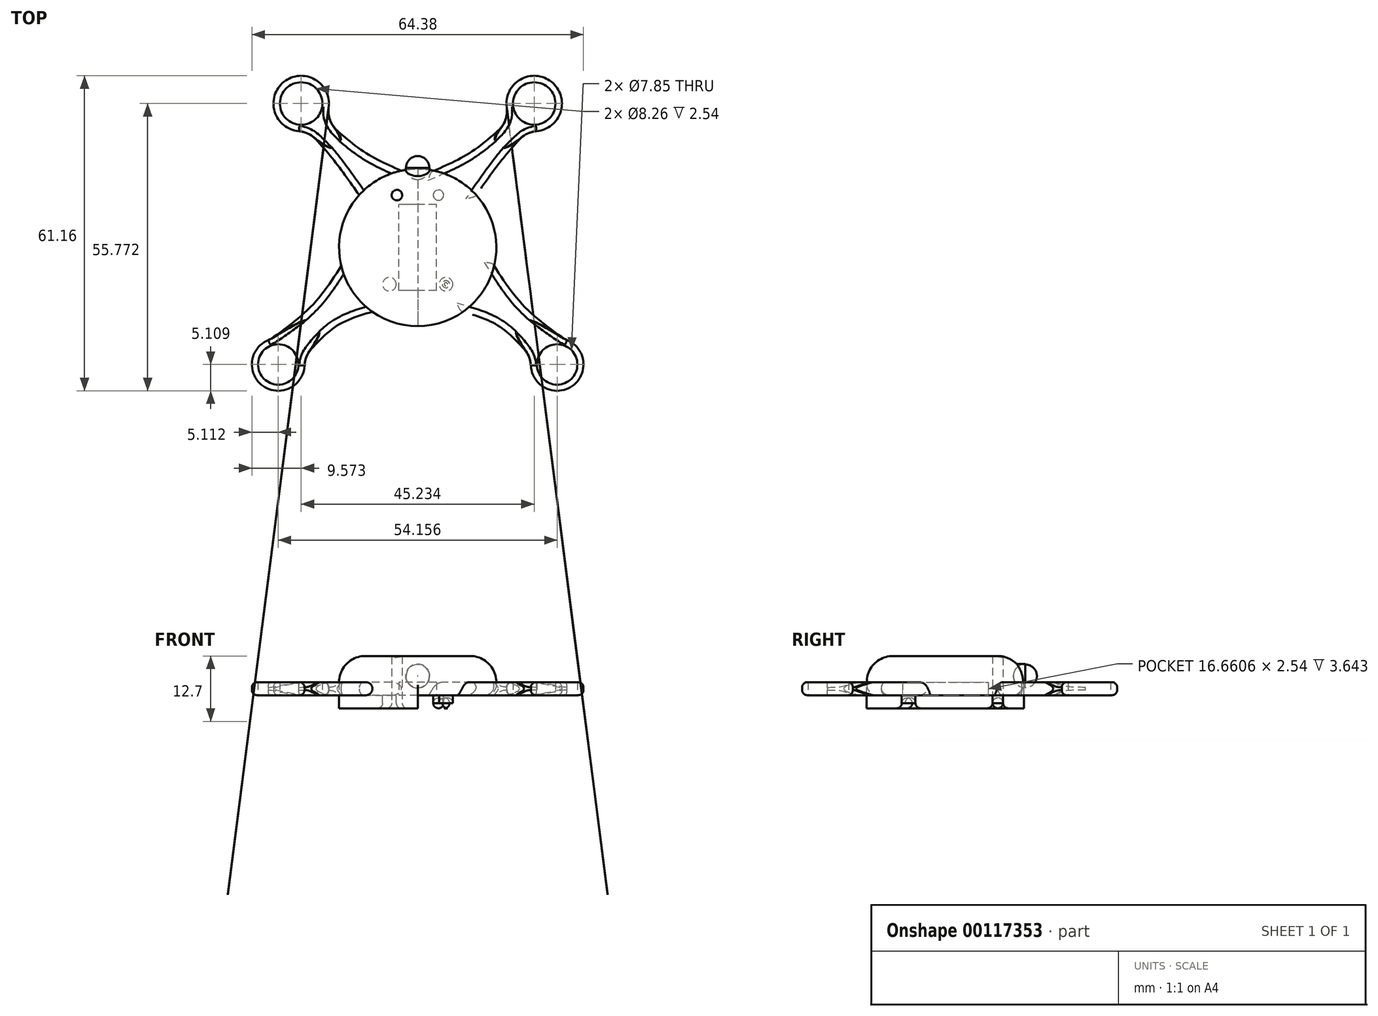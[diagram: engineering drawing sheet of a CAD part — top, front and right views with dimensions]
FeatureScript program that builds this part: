
annotation { "Feature Type Name" : "Feature", "Feature Type Description" : "" }
export const myFeature = defineFeature(function(context is Context, id is Id, definition is map)
    precondition{}
    {
        {
            var Q0;
            Q0=qCreatedBy(makeId("Top.planeOp"),FACE);
            var sketch = newSketch(context, id + "F0", { "sketchPlane" : qUnion([Q0])});
            skCircle(sketch, "E0", {"center": v(0, 0) * mm, "radius": 15.26 * mm});
            skLineSegment(sketch, "E1", {"start": v(9.1, 12.24) * mm, "end": v(22.62, 27.96) * mm});
            skCircle(sketch, "E2", {"center": v(22.62, 27.96) * mm, "radius": 5.39 * mm});
            skLineSegment(sketch, "E3", {"start": v(12.36, -8.95) * mm, "end": v(27.08, -22.7) * mm});
            skCircle(sketch, "E4", {"center": v(27.08, -22.7) * mm, "radius": 5.1 * mm});
            skFitSpline(sketch, "E5", {"points": [v(3.15, 14.93) * mm, v(10.13, 18.4) * mm, v(18.14, 24.96) * mm], "startDerivative": vector(15.03, 6.4) * mm, "endDerivative": vector(14.97, 13.52) * mm});
            skFitSpline(sketch, "E6", {"points": [v(11.37, 10.18) * mm, v(16.5, 17.24) * mm, v(21.38, 22.72) * mm], "startDerivative": vector(9.78, 14.08) * mm, "endDerivative": vector(10.27, 10.98) * mm});
            skFitSpline(sketch, "E7", {"points": [v(14.84, -3.54) * mm, v(20.44, -11.18) * mm, v(28.53, -17.8) * mm], "startDerivative": vector(10.46, -16.33) * mm, "endDerivative": vector(16.89, -12.25) * mm});
            skFitSpline(sketch, "E8", {"points": [v(8.8, -12.47) * mm, v(15.72, -15.22) * mm, v(22.14, -21.38) * mm], "startDerivative": vector(15.02, -4.3) * mm, "endDerivative": vector(11.73, -13.38) * mm});
            skCircle(sketch, "E9", {"center": v(4.03, 10.18) * mm, "radius": 1.02 * mm});
            skCircle(sketch, "E10", {"center": v(5.49, -7.13) * mm, "radius": 1.33 * mm});
            skLineSegment(sketch, "E11", {"start": v(0, 32.08) * mm, "end": v(0, -24.83) * mm});
            skFitSpline(sketch, "E12.MirrorCS", {"points": [v(-3.15, 14.93) * mm, v(-10.13, 18.4) * mm, v(-18.14, 24.96) * mm], "startDerivative": vector(-15.03, 6.4) * mm, "endDerivative": vector(-14.97, 13.52) * mm});
            skCircle(sketch, "E13.MirrorC", {"center": v(-22.62, 27.96) * mm, "radius": 5.39 * mm});
            skFitSpline(sketch, "E14.MirrorCS", {"points": [v(-14.84, -3.54) * mm, v(-20.44, -11.18) * mm, v(-28.53, -17.8) * mm], "startDerivative": vector(-10.46, -16.33) * mm, "endDerivative": vector(-16.89, -12.25) * mm});
            skLineSegment(sketch, "E15.MirrorCS", {"start": v(-12.36, -8.95) * mm, "end": v(-27.08, -22.7) * mm});
            skFitSpline(sketch, "E16.MirrorCS", {"points": [v(-8.8, -12.47) * mm, v(-15.72, -15.22) * mm, v(-22.14, -21.38) * mm], "startDerivative": vector(-15.02, -4.3) * mm, "endDerivative": vector(-11.73, -13.38) * mm});
            skCircle(sketch, "E17.MirrorC", {"center": v(-27.08, -22.7) * mm, "radius": 5.1 * mm});
            skLineSegment(sketch, "E18.MirrorCS", {"start": v(-9.1, 12.24) * mm, "end": v(-22.62, 27.96) * mm});
            skFitSpline(sketch, "E19.MirrorCS", {"points": [v(-11.37, 10.18) * mm, v(-16.5, 17.24) * mm, v(-21.38, 22.72) * mm], "startDerivative": vector(-9.78, 14.08) * mm, "endDerivative": vector(-10.27, 10.98) * mm});
            skCircle(sketch, "E20.MirrorC", {"center": v(-5.49, -7.13) * mm, "radius": 1.33 * mm});
            skCircle(sketch, "E21.MirrorC", {"center": v(-4.03, 10.18) * mm, "radius": 1.02 * mm});
            skCircle(sketch, "E22", {"center": v(27.08, -22.7) * mm, "radius": 3.93 * mm});
            skCircle(sketch, "E23", {"center": v(22.62, 27.96) * mm, "radius": 4.13 * mm});
            skCircle(sketch, "E24.MirrorC", {"center": v(-22.62, 27.96) * mm, "radius": 4.13 * mm});
            skCircle(sketch, "E25.MirrorC", {"center": v(-27.08, -22.7) * mm, "radius": 3.93 * mm});
            skSolve(sketch);
        }
        {
            var Q0;
            Q0=makeQuery(id+"F0.imprint","IMPRINT",FACE,{"disambiguationData":[TD([[makeQuery(id+"F0.imprint","IMPRINT",EDGE,{"derivedFrom":sQuery(id+"F0.wireOp",EDGE,"E9")}),-1.0]])]});
            var Q1;
            Q1=makeQuery(id+"F0.imprint","IMPRINT",FACE,{"disambiguationData":[TD([[makeQuery(id+"F0.imprint","IMPRINT",EDGE,{"derivedFrom":sQuery(id+"F0.wireOp",EDGE,"E20.MirrorC")}),1.0]])]});
            var Q2;
            Q2=makeQuery(id+"F0.imprint","IMPRINT",FACE,{"disambiguationData":[TD([[makeQuery(id+"F0.imprint","IMPRINT",EDGE,{"derivedFrom":sQuery(id+"F0.wireOp",EDGE,"E9")}),1.0]])]});
            var Q3;
            Q3=makeQuery(id+"F0.imprint","IMPRINT",FACE,{"disambiguationData":[TD([[makeQuery(id+"F0.imprint","IMPRINT",EDGE,{"derivedFrom":sQuery(id+"F0.wireOp",EDGE,"E21.MirrorC")}),-1.0]])]});
            var Q4;
            Q4=makeQuery(id+"F0.imprint","IMPRINT",FACE,{"disambiguationData":[TD([[makeQuery(id+"F0.imprint","IMPRINT",EDGE,{"derivedFrom":sQuery(id+"F0.wireOp",EDGE,"E20.MirrorC")}),-1.0]])]});
            var Q5;
            Q5=makeQuery(id+"F0.imprint","IMPRINT",FACE,{"disambiguationData":[TD([[makeQuery(id+"F0.imprint","IMPRINT",EDGE,{"derivedFrom":sQuery(id+"F0.wireOp",EDGE,"E10")}),1.0]])]});
            extrude(context, id + "F1", {"entities" : qUnion([Q0, Q1, Q2, Q3, Q4, Q5]), "depth" : 7.62 * mm});
        }
        {
            var Q0;
            Q0 = qSketchRegion(id + "F0", true);
            extrude(context, id + "F2", {"entities" : qUnion([Q0]), "operationType" : NewBodyOperationType.ADD, "depth" : 2.54 * mm});
        }
        {
            var Q0;
            Q0=makeQuery(id+"F0.imprint","IMPRINT",FACE,{"disambiguationData":[TD([[makeQuery(id+"F0.imprint","IMPRINT",EDGE,{"derivedFrom":sQuery(id+"F0.wireOp",EDGE,"E10")}),1.0]])]});
            var Q1;
            Q1=makeQuery(id+"F0.imprint","IMPRINT",FACE,{"disambiguationData":[TD([[makeQuery(id+"F0.imprint","IMPRINT",EDGE,{"derivedFrom":sQuery(id+"F0.wireOp",EDGE,"E9")}),1.0]])]});
            var Q2;
            Q2=makeQuery(id+"F0.imprint","IMPRINT",FACE,{"disambiguationData":[TD([[makeQuery(id+"F0.imprint","IMPRINT",EDGE,{"derivedFrom":sQuery(id+"F0.wireOp",EDGE,"E21.MirrorC")}),-1.0]])]});
            var Q3;
            Q3=makeQuery(id+"F0.imprint","IMPRINT",FACE,{"disambiguationData":[TD([[makeQuery(id+"F0.imprint","IMPRINT",EDGE,{"derivedFrom":sQuery(id+"F0.wireOp",EDGE,"E20.MirrorC")}),-1.0]])]});
            extrude(context, id + "F3", {"entities" : qUnion([Q0, Q1, Q2, Q3]), "operationType" : NewBodyOperationType.ADD, "oppositeDirection" : true, "depth" : 2.54 * mm});
        }
        {
            var Q0;
            Q0=makeQuery(id+"F1.opExtrude","CAP_EDGE",EDGE,{"disambiguationData":[OSD([sQuery(id+"F0.wireOp",EDGE,"E0")])],"isStart":false});
            fillet(context, id + "F4", {"entities" : qUnion([Q0]), "radius" : 5.08 * mm, "tangentPropagation" : true, "allowEdgeOverflow" : false});
        }
        {
            var Q0;
            Q0=makeQuery(id+"F2.opExtrude","CAP_EDGE",EDGE,{"disambiguationData":[OSD([sQuery(id+"F0.wireOp",EDGE,"E12.MirrorCS")])],"isStart":false});
            var Q1;
            Q1=makeQuery(id+"F2.opExtrude","CAP_EDGE",EDGE,{"disambiguationData":[OSD([sQuery(id+"F0.wireOp",EDGE,"E19.MirrorCS")])],"isStart":false});
            var Q2;
            Q2=makeQuery(id+"F2.opExtrude","CAP_EDGE",EDGE,{"disambiguationData":[OSD([sQuery(id+"F0.wireOp",EDGE,"E6")])],"isStart":false});
            var Q3;
            Q3=makeQuery(id+"F2.opExtrude","CAP_EDGE",EDGE,{"disambiguationData":[OSD([sQuery(id+"F0.wireOp",EDGE,"E5")])],"isStart":false});
            var Q4;
            Q4=makeQuery(id+"F2.opExtrude","CAP_EDGE",EDGE,{"disambiguationData":[OSD([sQuery(id+"F0.wireOp",EDGE,"E8")])],"isStart":false});
            var Q5;
            Q5=makeQuery(id+"F2.opExtrude","CAP_EDGE",EDGE,{"disambiguationData":[OSD([sQuery(id+"F0.wireOp",EDGE,"E7")])],"isStart":false});
            var Q6;
            Q6=makeQuery(id+"F2.opExtrude","CAP_EDGE",EDGE,{"disambiguationData":[OSD([sQuery(id+"F0.wireOp",EDGE,"E16.MirrorCS")])],"isStart":false});
            var Q7;
            Q7=makeQuery(id+"F2.opExtrude","CAP_EDGE",EDGE,{"disambiguationData":[OSD([sQuery(id+"F0.wireOp",EDGE,"E14.MirrorCS")])],"isStart":false});
            var Q8;
            Q8=makeQuery(id+"F2.opExtrude","CAP_EDGE",EDGE,{"disambiguationData":[OSD([sQuery(id+"F0.wireOp",EDGE,"E12.MirrorCS")])],"isStart":true});
            var Q9;
            Q9=makeQuery(id+"F2.opExtrude","CAP_EDGE",EDGE,{"disambiguationData":[OSD([sQuery(id+"F0.wireOp",EDGE,"E5")])],"isStart":true});
            var Q10;
            Q10=makeQuery(id+"F2.opExtrude","CAP_EDGE",EDGE,{"disambiguationData":[OSD([sQuery(id+"F0.wireOp",EDGE,"E14.MirrorCS")])],"isStart":true});
            var Q11;
            Q11=makeQuery(id+"F2.opExtrude","CAP_EDGE",EDGE,{"disambiguationData":[OSD([sQuery(id+"F0.wireOp",EDGE,"E7")])],"isStart":true});
            var Q12;
            Q12=makeQuery(id+"F2.opExtrude","CAP_EDGE",EDGE,{"disambiguationData":[OSD([sQuery(id+"F0.wireOp",EDGE,"E6")])],"isStart":true});
            var Q13;
            Q13=makeQuery(id+"F2.opExtrude","CAP_EDGE",EDGE,{"disambiguationData":[OSD([sQuery(id+"F0.wireOp",EDGE,"E8")])],"isStart":true});
            var Q14;
            Q14=makeQuery(id+"F2.opExtrude","CAP_EDGE",EDGE,{"disambiguationData":[OSD([sQuery(id+"F0.wireOp",EDGE,"E16.MirrorCS")])],"isStart":true});
            var Q15;
            Q15=makeQuery(id+"F2.opExtrude","CAP_EDGE",EDGE,{"disambiguationData":[OSD([sQuery(id+"F0.wireOp",EDGE,"E19.MirrorCS")])],"isStart":true});
            fillet(context, id + "F5", {"entities" : qUnion([Q0, Q1, Q2, Q3, Q4, Q5, Q6, Q7, Q8, Q9, Q10, Q11, Q12, Q13, Q14, Q15]), "radius" : 1.27 * mm, "tangentPropagation" : true, "allowEdgeOverflow" : false});
        }
        {
            var Q0;
            {var subQ0=sQuery(id+"F0.wireOp",EDGE,"E5");var subQ2=sQuery(id+"F0.wireOp",EDGE,"E0");Q0=makeQuery(id+"F2.boolean.opBoolean","SPLIT",EDGE,{"disambiguationData":[TD([makeQuery(id+"F2.opExtrude","SWEPT_FACE",FACE,{"disambiguationData":[OSD([subQ0])]})])],"derivedFrom":makeQuery(id+"F1.opExtrude","CAP_EDGE",EDGE,{"disambiguationData":[OSD([subQ2])],"isStart":true})});}
            var Q1;
            {var subQ0=sQuery(id+"F0.wireOp",EDGE,"E6");var subQ2=sQuery(id+"F0.wireOp",EDGE,"E0");Q1=makeQuery(id+"F2.boolean.opBoolean","SPLIT",EDGE,{"disambiguationData":[TD([makeQuery(id+"F2.opExtrude","SWEPT_FACE",FACE,{"disambiguationData":[OSD([subQ0])]})])],"derivedFrom":makeQuery(id+"F1.opExtrude","CAP_EDGE",EDGE,{"disambiguationData":[OSD([subQ2])],"isStart":true})});}
            var Q2;
            {var subQ0=sQuery(id+"F0.wireOp",EDGE,"E8");var subQ2=sQuery(id+"F0.wireOp",EDGE,"E0");Q2=makeQuery(id+"F2.boolean.opBoolean","SPLIT",EDGE,{"disambiguationData":[TD([makeQuery(id+"F2.opExtrude","SWEPT_FACE",FACE,{"disambiguationData":[OSD([subQ0])]})])],"derivedFrom":makeQuery(id+"F1.opExtrude","CAP_EDGE",EDGE,{"disambiguationData":[OSD([subQ2])],"isStart":true})});}
            var Q3;
            {var subQ0=sQuery(id+"F0.wireOp",EDGE,"E14.MirrorCS");var subQ2=sQuery(id+"F0.wireOp",EDGE,"E0");Q3=makeQuery(id+"F2.boolean.opBoolean","SPLIT",EDGE,{"disambiguationData":[TD([makeQuery(id+"F2.opExtrude","SWEPT_FACE",FACE,{"disambiguationData":[OSD([subQ0])]})])],"derivedFrom":makeQuery(id+"F1.opExtrude","CAP_EDGE",EDGE,{"disambiguationData":[OSD([subQ2])],"isStart":true})});}
            fillet(context, id + "F6", {"entities" : qUnion([Q0, Q1, Q2, Q3]), "radius" : 2.03 * mm, "tangentPropagation" : true, "allowEdgeOverflow" : false});
        }
        {
            var Q0;
            Q0=makeQuery(id+"F3.opExtrude","CAP_EDGE",EDGE,{"disambiguationData":[OSD([sQuery(id+"F0.wireOp",EDGE,"E21.MirrorC")])],"isStart":false});
            var Q1;
            Q1=makeQuery(id+"F3.opExtrude","CAP_EDGE",EDGE,{"disambiguationData":[OSD([sQuery(id+"F0.wireOp",EDGE,"E20.MirrorC")])],"isStart":false});
            var Q2;
            Q2=makeQuery(id+"F3.opExtrude","CAP_EDGE",EDGE,{"disambiguationData":[OSD([sQuery(id+"F0.wireOp",EDGE,"E9")])],"isStart":false});
            var Q3;
            Q3=makeQuery(id+"F3.opExtrude","CAP_EDGE",EDGE,{"disambiguationData":[OSD([sQuery(id+"F0.wireOp",EDGE,"E10")])],"isStart":false});
            fillet(context, id + "F7", {"entities" : qUnion([Q0, Q1, Q2, Q3]), "radius" : 1.02 * mm, "tangentPropagation" : true, "allowEdgeOverflow" : false});
        }
        {
            var Q0;
            Q0=makeQuery(id+"F5.opFillet","BLEND_EDGE",EDGE,{"blendedFrom":[makeQuery(id+"F2.opExtrude","CAP_EDGE",EDGE,{"disambiguationData":[OSD([sQuery(id+"F0.wireOp",EDGE,"E12.MirrorCS")])],"isStart":true}),makeQuery(id+"F2.opExtrude","SWEPT_FACE",FACE,{"disambiguationData":[OSD([sQuery(id+"F0.wireOp",EDGE,"E13.MirrorC")])]})],"blendedInto":[makeQuery(id+"F2.opExtrude","SWEPT_FACE",FACE,{"disambiguationData":[OSD([sQuery(id+"F0.wireOp",EDGE,"E13.MirrorC")])]})]});
            var Q1;
            Q1=makeQuery(id+"F5.opFillet","BLEND_EDGE",EDGE,{"blendedFrom":[makeQuery(id+"F2.opExtrude","CAP_EDGE",EDGE,{"disambiguationData":[OSD([sQuery(id+"F0.wireOp",EDGE,"E19.MirrorCS")])],"isStart":true}),makeQuery(id+"F2.opExtrude","SWEPT_FACE",FACE,{"disambiguationData":[OSD([sQuery(id+"F0.wireOp",EDGE,"E13.MirrorC")])]})],"blendedInto":[makeQuery(id+"F2.opExtrude","SWEPT_FACE",FACE,{"disambiguationData":[OSD([sQuery(id+"F0.wireOp",EDGE,"E13.MirrorC")])]})]});
            var Q2;
            Q2=makeQuery(id+"F5.opFillet","BLEND_EDGE",EDGE,{"blendedFrom":[makeQuery(id+"F2.opExtrude","CAP_EDGE",EDGE,{"disambiguationData":[OSD([sQuery(id+"F0.wireOp",EDGE,"E14.MirrorCS")])],"isStart":true}),makeQuery(id+"F2.opExtrude","SWEPT_FACE",FACE,{"disambiguationData":[OSD([sQuery(id+"F0.wireOp",EDGE,"E17.MirrorC")])]})],"blendedInto":[makeQuery(id+"F2.opExtrude","SWEPT_FACE",FACE,{"disambiguationData":[OSD([sQuery(id+"F0.wireOp",EDGE,"E17.MirrorC")])]})]});
            var Q3;
            Q3=makeQuery(id+"F5.opFillet","BLEND_EDGE",EDGE,{"blendedFrom":[makeQuery(id+"F2.opExtrude","CAP_EDGE",EDGE,{"disambiguationData":[OSD([sQuery(id+"F0.wireOp",EDGE,"E5")])],"isStart":false}),makeQuery(id+"F2.opExtrude","SWEPT_FACE",FACE,{"disambiguationData":[OSD([sQuery(id+"F0.wireOp",EDGE,"E2")])]})],"blendedInto":[makeQuery(id+"F2.opExtrude","SWEPT_FACE",FACE,{"disambiguationData":[OSD([sQuery(id+"F0.wireOp",EDGE,"E2")])]})]});
            var Q4;
            Q4=makeQuery(id+"F5.opFillet","BLEND_EDGE",EDGE,{"blendedFrom":[makeQuery(id+"F2.opExtrude","CAP_EDGE",EDGE,{"disambiguationData":[OSD([sQuery(id+"F0.wireOp",EDGE,"E6")])],"isStart":false}),makeQuery(id+"F2.opExtrude","SWEPT_FACE",FACE,{"disambiguationData":[OSD([sQuery(id+"F0.wireOp",EDGE,"E2")])]})],"blendedInto":[makeQuery(id+"F2.opExtrude","SWEPT_FACE",FACE,{"disambiguationData":[OSD([sQuery(id+"F0.wireOp",EDGE,"E2")])]})]});
            var Q5;
            Q5=makeQuery(id+"F5.opFillet","BLEND_EDGE",EDGE,{"blendedFrom":[makeQuery(id+"F2.opExtrude","CAP_EDGE",EDGE,{"disambiguationData":[OSD([sQuery(id+"F0.wireOp",EDGE,"E16.MirrorCS")])],"isStart":false}),makeQuery(id+"F2.opExtrude","SWEPT_FACE",FACE,{"disambiguationData":[OSD([sQuery(id+"F0.wireOp",EDGE,"E17.MirrorC")])]})],"blendedInto":[makeQuery(id+"F2.opExtrude","SWEPT_FACE",FACE,{"disambiguationData":[OSD([sQuery(id+"F0.wireOp",EDGE,"E17.MirrorC")])]})]});
            var Q6;
            Q6=makeQuery(id+"F5.opFillet","BLEND_EDGE",EDGE,{"blendedFrom":[makeQuery(id+"F2.opExtrude","CAP_EDGE",EDGE,{"disambiguationData":[OSD([sQuery(id+"F0.wireOp",EDGE,"E7")])],"isStart":false}),makeQuery(id+"F2.opExtrude","SWEPT_FACE",FACE,{"disambiguationData":[OSD([sQuery(id+"F0.wireOp",EDGE,"E4")])]})],"blendedInto":[makeQuery(id+"F2.opExtrude","SWEPT_FACE",FACE,{"disambiguationData":[OSD([sQuery(id+"F0.wireOp",EDGE,"E4")])]})]});
            var Q7;
            Q7=makeQuery(id+"F5.opFillet","BLEND_EDGE",EDGE,{"blendedFrom":[makeQuery(id+"F2.opExtrude","CAP_EDGE",EDGE,{"disambiguationData":[OSD([sQuery(id+"F0.wireOp",EDGE,"E8")])],"isStart":false}),makeQuery(id+"F2.opExtrude","SWEPT_FACE",FACE,{"disambiguationData":[OSD([sQuery(id+"F0.wireOp",EDGE,"E4")])]})],"blendedInto":[makeQuery(id+"F2.opExtrude","SWEPT_FACE",FACE,{"disambiguationData":[OSD([sQuery(id+"F0.wireOp",EDGE,"E4")])]})]});
            fillet(context, id + "F8", {"entities" : qUnion([Q0, Q1, Q2, Q3, Q4, Q5, Q6, Q7]), "radius" : 5.08 * mm, "tangentPropagation" : true, "allowEdgeOverflow" : false});
        }
        {
            var Q0;
            Q0=makeQuery(id+"F2.opExtrude","CAP_EDGE",EDGE,{"disambiguationData":[OSD([sQuery(id+"F0.wireOp",EDGE,"E13.MirrorC")])],"isStart":false});
            var Q1;
            Q1=makeQuery(id+"F2.opExtrude","CAP_EDGE",EDGE,{"disambiguationData":[OSD([sQuery(id+"F0.wireOp",EDGE,"E13.MirrorC")])],"isStart":true});
            var Q2;
            Q2=makeQuery(id+"F2.opExtrude","CAP_EDGE",EDGE,{"disambiguationData":[OSD([sQuery(id+"F0.wireOp",EDGE,"E17.MirrorC")])],"isStart":false});
            var Q3;
            Q3=makeQuery(id+"F2.opExtrude","CAP_EDGE",EDGE,{"disambiguationData":[OSD([sQuery(id+"F0.wireOp",EDGE,"E4")])],"isStart":false});
            var Q4;
            Q4=makeQuery(id+"F2.opExtrude","CAP_EDGE",EDGE,{"disambiguationData":[OSD([sQuery(id+"F0.wireOp",EDGE,"E2")])],"isStart":false});
            var Q5;
            Q5=makeQuery(id+"F2.opExtrude","CAP_EDGE",EDGE,{"disambiguationData":[OSD([sQuery(id+"F0.wireOp",EDGE,"E2")])],"isStart":true});
            var Q6;
            Q6=makeQuery(id+"F2.opExtrude","CAP_EDGE",EDGE,{"disambiguationData":[OSD([sQuery(id+"F0.wireOp",EDGE,"E17.MirrorC")])],"isStart":true});
            var Q7;
            Q7=makeQuery(id+"F2.opExtrude","CAP_EDGE",EDGE,{"disambiguationData":[OSD([sQuery(id+"F0.wireOp",EDGE,"E4")])],"isStart":true});
            fillet(context, id + "F9", {"entities" : qUnion([Q0, Q1, Q2, Q3, Q4, Q5, Q6, Q7]), "radius" : 1.02 * mm, "tangentPropagation" : true, "allowEdgeOverflow" : false});
        }
        {
            var Q0;
            Q0=qCreatedBy(makeId("Front.planeOp"),FACE);
            var sketch = newSketch(context, id + "F10", { "sketchPlane" : qUnion([Q0])});
            skCircle(sketch, "E26", {"center": v(0, 3.73) * mm, "radius": 2.32 * mm});
            skSolve(sketch);
        }
        {
            var Q0;
            Q0=makeQuery(id+"F10.imprint","IMPRINT",FACE,{"disambiguationData":[TD([[makeQuery(id+"F10.imprint","IMPRINT",EDGE,{"derivedFrom":sQuery(id+"F10.wireOp",EDGE,"E26")}),1.0]])]});
            extrude(context, id + "F11", {"entities" : qUnion([Q0]), "operationType" : NewBodyOperationType.ADD, "oppositeDirection" : true, "depth" : 17.78 * mm});
        }
        {
            var Q0;
            Q0=makeQuery(id+"F11.opExtrude","CAP_EDGE",EDGE,{"disambiguationData":[OSD([sQuery(id+"F10.wireOp",EDGE,"E26")])],"isStart":false});
            fillet(context, id + "F12", {"entities" : qUnion([Q0]), "radius" : 2.3 * mm, "tangentPropagation" : true, "allowEdgeOverflow" : false});
        }
        {
            var Q0;
            Q0=qCreatedBy(makeId("Top.planeOp"),FACE);
            var sketch = newSketch(context, id + "F13", { "sketchPlane" : qUnion([Q0])});
            skLineSegment(sketch, "E27.bottom", {"start": v(3.64, -8.33) * mm, "end": v(-3.64, -8.33) * mm});
            skLineSegment(sketch, "E27.top", {"start": v(3.64, 8.33) * mm, "end": v(-3.64, 8.33) * mm});
            skLineSegment(sketch, "E27.left", {"start": v(3.64, -8.33) * mm, "end": v(3.64, 8.33) * mm});
            skLineSegment(sketch, "E27.right", {"start": v(-3.64, -8.33) * mm, "end": v(-3.64, 8.33) * mm});
            skPoint(sketch, "E27.middle", {"position": v(0, 0) * mm});
            skSolve(sketch);
        }
        {
            var Q0;
            Q0=makeQuery(id+"F13.imprint","IMPRINT",FACE,{"disambiguationData":[TD([[makeQuery(id+"F13.imprint","IMPRINT",EDGE,{"derivedFrom":sQuery(id+"F13.wireOp",EDGE,"E27.bottom")}),-1.0]])]});
            extrude(context, id + "F14", {"entities" : qUnion([Q0]), "operationType" : NewBodyOperationType.REMOVE, "depth" : 2.54 * mm});
        }
    });
